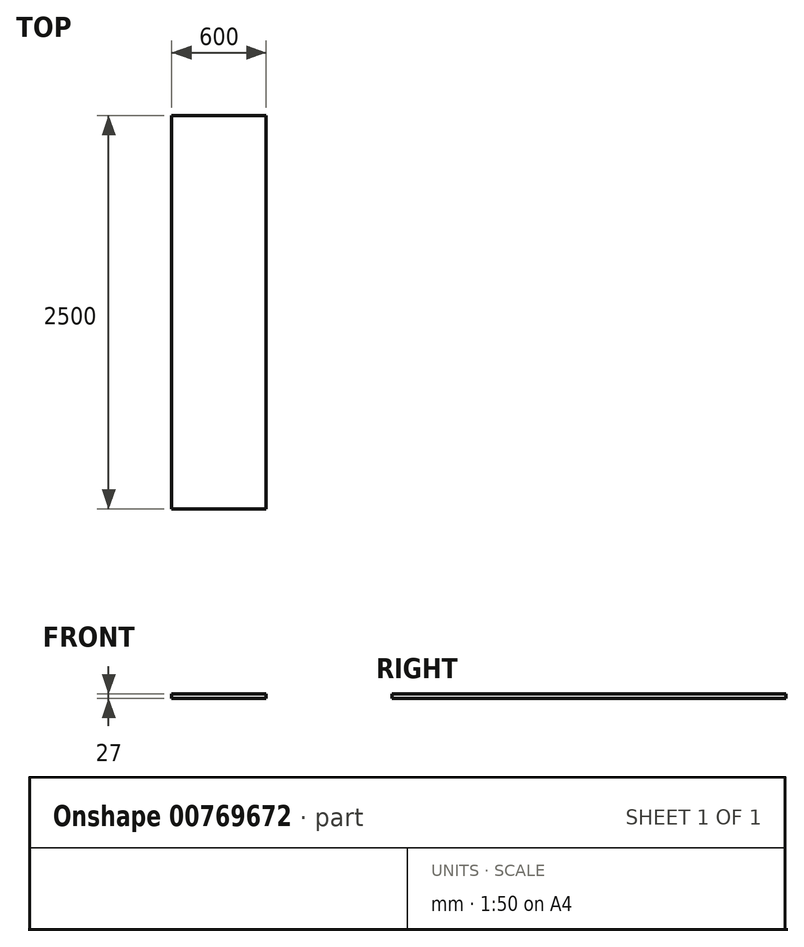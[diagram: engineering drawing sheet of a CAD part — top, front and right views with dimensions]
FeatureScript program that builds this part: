
annotation { "Feature Type Name" : "Feature", "Feature Type Description" : "" }
export const myFeature = defineFeature(function(context is Context, id is Id, definition is map)
    precondition{}
    {
        {
            var Q0;
            Q0=qCreatedBy(makeId("Front.planeOp"),FACE);
            var sketch = newSketch(context, id + "F0", { "sketchPlane" : qUnion([Q0])});
            skLineSegment(sketch, "E0.bottom", {"start": v(-80.39, 13.28) * mm, "end": v(519.61, 13.28) * mm});
            skLineSegment(sketch, "E0.top", {"start": v(-80.39, -13.72) * mm, "end": v(519.61, -13.72) * mm});
            skLineSegment(sketch, "E0.left", {"start": v(-80.39, 13.28) * mm, "end": v(-80.39, -13.72) * mm});
            skLineSegment(sketch, "E0.right", {"start": v(519.61, 13.28) * mm, "end": v(519.61, -13.72) * mm});
            skSolve(sketch);
        }
        {
            var Q0;
            Q0=makeQuery(id+"F0.imprint","IMPRINT",FACE,{"disambiguationData":[TD([[makeQuery(id+"F0.imprint","IMPRINT",EDGE,{"derivedFrom":sQuery(id+"F0.wireOp",EDGE,"E0.bottom")}),-1.0]])]});
            extrude(context, id + "F1", {"entities" : qUnion([Q0]), "depth" : 2500 * mm, "offsetDistance" : 25 * mm});
        }
    });
